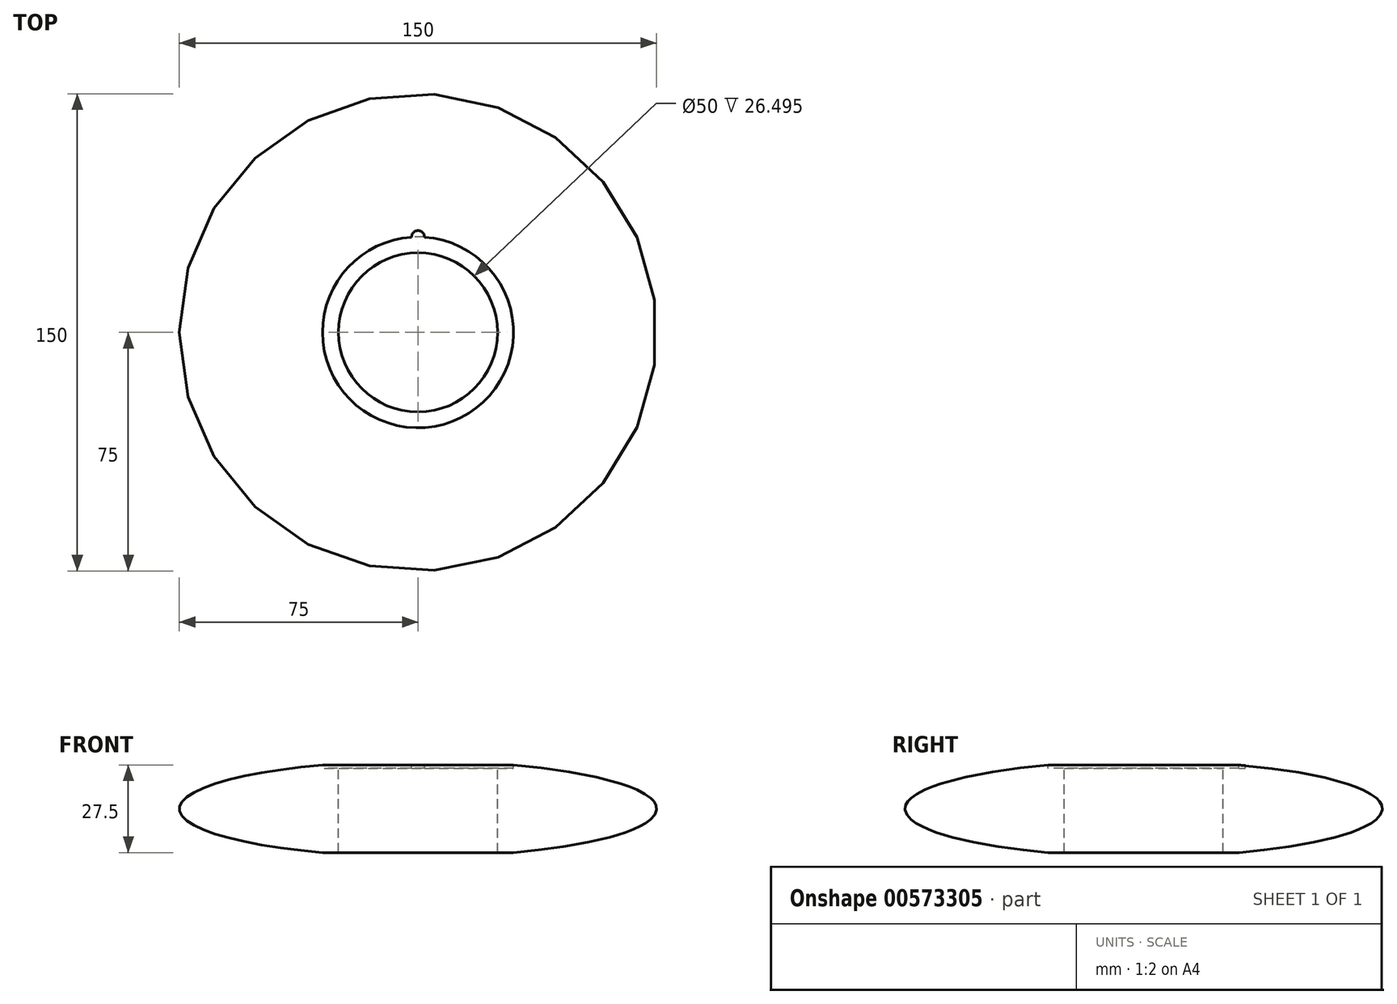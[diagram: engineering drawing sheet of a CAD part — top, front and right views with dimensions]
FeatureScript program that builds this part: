
annotation { "Feature Type Name" : "Feature", "Feature Type Description" : "" }
export const myFeature = defineFeature(function(context is Context, id is Id, definition is map)
    precondition{}
    {
        {
            var Q0;
            Q0=qCreatedBy(makeId("Front.planeOp"),FACE);
            var sketch = newSketch(context, id + "F0", { "sketchPlane" : qUnion([Q0])});
            skEllipticalArc(sketch, "E0", {});
            skLineSegment(sketch, "E1", {"start": v(0, -13.75) * mm, "end": v(0, 13.75) * mm});
            skLineSegment(sketch, "E2", {"start": v(-30, 13.75) * mm, "end": v(0, 13.75) * mm});
            skLineSegment(sketch, "E3", {"start": v(-30, -13.75) * mm, "end": v(0, -13.75) * mm});
            skPoint(sketch, "E4.orphan", {"position": v(0, -15) * mm});
            skPoint(sketch, "E5.orphan", {"position": v(0, 15) * mm});
            const initialGuessF0  = {"E0": [0, 0, 1, 0, 0.075, 0.015, 1.9823131728623844, 4.300872134317206]};
            skSetInitialGuess(sketch, initialGuessF0);
            skSolve(sketch);
        }
        {
            var Q0;
            Q0=makeQuery(id+"F0.imprint","IMPRINT",FACE,{"disambiguationData":[TD([[makeQuery(id+"F0.imprint","IMPRINT",EDGE,{"derivedFrom":sQuery(id+"F0.wireOp",EDGE,"E0")}),1.0]])]});
            var Q1;
            Q1=sQuery(id+"F0.wireOp",EDGE,"E1");
            revolve(context, id + "F1", {"entities" : qUnion([Q0]), "axis" : qUnion([Q1]), "revolveType" : RevolveType.FULL});
        }
        {
            var Q0;
            Q0=makeQuery(id+"F1.opRevolve","SWEPT_FACE",FACE,{"disambiguationData":[OSD([sQuery(id+"F0.wireOp",EDGE,"E2")])]});
            var sketch = newSketch(context, id + "F2", { "sketchPlane" : qUnion([Q0])});
            skCircle(sketch, "E6", {"center": v(0, 0) * mm, "radius": 25 * mm});
            skLineSegment(sketch, "E7", {"start": v(0, 0) * mm, "end": v(0, 25) * mm, "construction": true});
            skLineSegment(sketch, "E8", {"start": v(0, 0) * mm, "end": v(25, 0) * mm, "construction": true});
            skSolve(sketch);
        }
        {
            var Q0;
            Q0=sQuery(id+"F2.wireOp",VERTEX,"E7.end");
            var Q1;
            Q1=sQuery(id+"F2.wireOp",VERTEX,"E6.center");
            var Q2;
            Q2=sQuery(id+"F2.wireOp",VERTEX,"E8.end");
            cPlane(context, id + "F3", {"entities" : qUnion([Q0, Q1, Q2]), "cplaneType" : CPlaneType.THREE_POINT, "offset" : 25 * mm, "width" : 150 * mm, "height" : 150 * mm});
        }
        {
            var Q0;
            Q0=makeQuery(id+"F2.imprint","IMPRINT",FACE,{"disambiguationData":[TD([[makeQuery(id+"F2.imprint","IMPRINT",EDGE,{"derivedFrom":sQuery(id+"F2.wireOp",EDGE,"E6")}),1.0]])]});
            extrude(context, id + "F4", {"entities" : qUnion([Q0]), "operationType" : NewBodyOperationType.REMOVE, "endBound" : BoundingType.UP_TO_NEXT, "oppositeDirection" : true, "depth" : 25 * mm, "offsetDistance" : 25 * mm});
        }
        {
            var Q0;
            Q0=makeQuery(id+"F1.opRevolve","SWEPT_FACE",FACE,{"disambiguationData":[OSD([sQuery(id+"F0.wireOp",EDGE,"E2")])]});
            extrude(context, id + "F5", {"entities" : qUnion([Q0]), "operationType" : NewBodyOperationType.REMOVE, "oppositeDirection" : true, "depth" : 1 * mm, "offsetDistance" : 25 * mm});
        }
        {
            var Q0;
            Q0=qCreatedBy(id+"F3.planeOp",FACE);
            var sketch = newSketch(context, id + "F6", { "sketchPlane" : qUnion([Q0])});
            skArc(sketch, "E9.0", {"start": v(-2, -29.93) * mm, "mid": v(0, -30) * mm, "end": v(2, -29.93) * mm});
            skArc(sketch, "E10", {"start": v(-2, -29.93) * mm, "mid": v(0, -32) * mm, "end": v(2, -29.93) * mm});
            skSolve(sketch);
        }
        {
            var Q0;
            Q0=makeQuery(id+"F6.imprint","IMPRINT",FACE,{"disambiguationData":[TD([[makeQuery(id+"F6.imprint","IMPRINT",EDGE,{"derivedFrom":sQuery(id+"F6.wireOp",EDGE,"E9.0")}),-1.0]])]});
            extrude(context, id + "F7", {"entities" : qUnion([Q0]), "operationType" : NewBodyOperationType.REMOVE, "depth" : 1 * mm, "offsetDistance" : 25 * mm});
        }
    });
